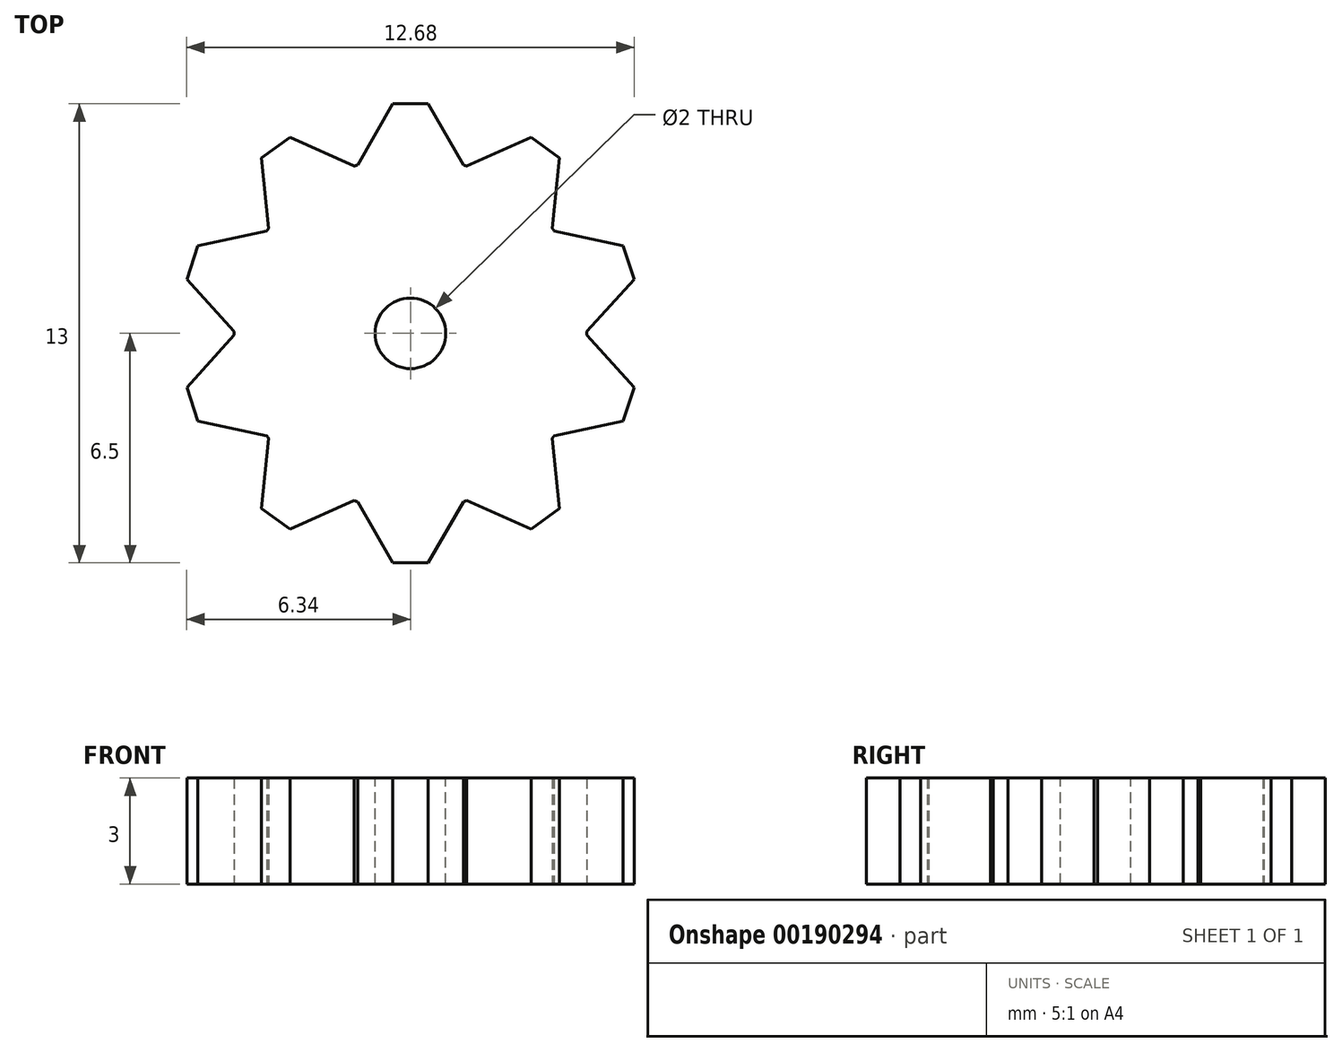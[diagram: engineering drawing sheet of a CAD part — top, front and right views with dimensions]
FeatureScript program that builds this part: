
annotation { "Feature Type Name" : "Feature", "Feature Type Description" : "" }
export const myFeature = defineFeature(function(context is Context, id is Id, definition is map)
    precondition{}
    {
        {
            var Q0;
            Q0=qCreatedBy(makeId("Top.planeOp"),FACE);
            var sketch = newSketch(context, id + "F0", { "sketchPlane" : qUnion([Q0])});
            skCircle(sketch, "E0", {"center": v(0, 0) * mm, "radius": 5 * mm});
            skLineSegment(sketch, "E1", {"start": v(0, 0) * mm, "end": v(0, 6.5) * mm, "construction": true});
            skLineSegment(sketch, "E2", {"start": v(0, 6.5) * mm, "end": v(-0.5, 6.5) * mm});
            skLineSegment(sketch, "E3", {"start": v(-0.5, 6.5) * mm, "end": v(-1.5, 4.77) * mm});
            skLineSegment(sketch, "E4.MirrorCS", {"start": v(0, 6.5) * mm, "end": v(0.5, 6.5) * mm});
            skLineSegment(sketch, "E5.MirrorCS", {"start": v(0.5, 6.5) * mm, "end": v(1.5, 4.77) * mm});
            skLineSegment(sketch, "E6.1.0", {"start": v(-4.23, 4.96) * mm, "end": v(-4.02, 2.98) * mm});
            skLineSegment(sketch, "E6.1.1", {"start": v(-3.82, 5.26) * mm, "end": v(-4.23, 4.96) * mm});
            skLineSegment(sketch, "E6.1.2", {"start": v(-3.82, 5.26) * mm, "end": v(-3.42, 5.55) * mm});
            skLineSegment(sketch, "E6.1.3", {"start": v(-3.42, 5.55) * mm, "end": v(-1.6, 4.74) * mm});
            skLineSegment(sketch, "E6.2.0", {"start": v(-6.34, 1.53) * mm, "end": v(-5, 0.05) * mm});
            skLineSegment(sketch, "E6.2.1", {"start": v(-6.18, 2) * mm, "end": v(-6.34, 1.53) * mm});
            skLineSegment(sketch, "E6.2.2", {"start": v(-6.18, 2) * mm, "end": v(-6.03, 2.48) * mm});
            skLineSegment(sketch, "E6.2.3", {"start": v(-6.03, 2.48) * mm, "end": v(-4.07, 2.9) * mm});
            skLineSegment(sketch, "E7.2.3.0", {"start": v(-6.03, -2.48) * mm, "end": v(-4.07, -2.9) * mm});
            skLineSegment(sketch, "E7.3.3.0", {"start": v(-6.18, -2) * mm, "end": v(-6.03, -2.48) * mm});
            skLineSegment(sketch, "E7.6.3.0", {"start": v(-6.18, -2) * mm, "end": v(-6.34, -1.53) * mm});
            skLineSegment(sketch, "E7.9.3.0", {"start": v(-6.34, -1.53) * mm, "end": v(-5, -0.05) * mm});
            skLineSegment(sketch, "E7.2.4.0", {"start": v(-3.42, -5.55) * mm, "end": v(-1.6, -4.74) * mm});
            skLineSegment(sketch, "E7.3.4.0", {"start": v(-3.82, -5.26) * mm, "end": v(-3.42, -5.55) * mm});
            skLineSegment(sketch, "E7.6.4.0", {"start": v(-3.82, -5.26) * mm, "end": v(-4.23, -4.96) * mm});
            skLineSegment(sketch, "E7.9.4.0", {"start": v(-4.23, -4.96) * mm, "end": v(-4.02, -2.98) * mm});
            skLineSegment(sketch, "E7.2.5.0", {"start": v(0.5, -6.5) * mm, "end": v(1.5, -4.77) * mm});
            skLineSegment(sketch, "E7.3.5.0", {"start": v(0, -6.5) * mm, "end": v(0.5, -6.5) * mm});
            skLineSegment(sketch, "E7.6.5.0", {"start": v(0, -6.5) * mm, "end": v(-0.5, -6.5) * mm});
            skLineSegment(sketch, "E7.9.5.0", {"start": v(-0.5, -6.5) * mm, "end": v(-1.5, -4.77) * mm});
            skLineSegment(sketch, "E7.2.6.0", {"start": v(4.23, -4.96) * mm, "end": v(4.02, -2.98) * mm});
            skLineSegment(sketch, "E7.3.6.0", {"start": v(3.82, -5.26) * mm, "end": v(4.23, -4.96) * mm});
            skLineSegment(sketch, "E7.6.6.0", {"start": v(3.82, -5.26) * mm, "end": v(3.42, -5.55) * mm});
            skLineSegment(sketch, "E7.9.6.0", {"start": v(3.42, -5.55) * mm, "end": v(1.6, -4.74) * mm});
            skLineSegment(sketch, "E7.2.7.0", {"start": v(6.34, -1.53) * mm, "end": v(5, -0.05) * mm});
            skLineSegment(sketch, "E7.3.7.0", {"start": v(6.18, -2) * mm, "end": v(6.34, -1.53) * mm});
            skLineSegment(sketch, "E7.6.7.0", {"start": v(6.18, -2) * mm, "end": v(6.03, -2.48) * mm});
            skLineSegment(sketch, "E7.9.7.0", {"start": v(6.03, -2.48) * mm, "end": v(4.07, -2.9) * mm});
            skLineSegment(sketch, "E7.2.8.0", {"start": v(6.03, 2.48) * mm, "end": v(4.07, 2.9) * mm});
            skLineSegment(sketch, "E7.3.8.0", {"start": v(6.18, 2) * mm, "end": v(6.03, 2.48) * mm});
            skLineSegment(sketch, "E7.6.8.0", {"start": v(6.18, 2) * mm, "end": v(6.34, 1.53) * mm});
            skLineSegment(sketch, "E7.9.8.0", {"start": v(6.34, 1.53) * mm, "end": v(5, 0.05) * mm});
            skLineSegment(sketch, "E7.2.9.0", {"start": v(3.42, 5.55) * mm, "end": v(1.6, 4.74) * mm});
            skLineSegment(sketch, "E7.3.9.0", {"start": v(3.82, 5.26) * mm, "end": v(3.42, 5.55) * mm});
            skLineSegment(sketch, "E7.6.9.0", {"start": v(3.82, 5.26) * mm, "end": v(4.23, 4.96) * mm});
            skLineSegment(sketch, "E7.9.9.0", {"start": v(4.23, 4.96) * mm, "end": v(4.02, 2.98) * mm});
            skSolve(sketch);
        }
        {
            var Q0;
            Q0 = qSketchRegion(id + "F0", true);
            extrude(context, id + "F1", {"entities" : qUnion([Q0]), "depth" : 3 * mm});
        }
        {
            var Q0;
            Q0=makeQuery(id+"F1.opExtrude","CAP_FACE",FACE,{"disambiguationData":[OSD([sQuery(id+"F0.wireOp",EDGE,"E0"),sQuery(id+"F0.wireOp",EDGE,"E2"),sQuery(id+"F0.wireOp",EDGE,"E3"),sQuery(id+"F0.wireOp",EDGE,"E4.MirrorCS"),sQuery(id+"F0.wireOp",EDGE,"E5.MirrorCS"),sQuery(id+"F0.wireOp",EDGE,"E6.1.0"),sQuery(id+"F0.wireOp",EDGE,"E6.1.1"),sQuery(id+"F0.wireOp",EDGE,"E6.1.2"),sQuery(id+"F0.wireOp",EDGE,"E6.1.3"),sQuery(id+"F0.wireOp",EDGE,"E6.2.0"),sQuery(id+"F0.wireOp",EDGE,"E6.2.1"),sQuery(id+"F0.wireOp",EDGE,"E6.2.2"),sQuery(id+"F0.wireOp",EDGE,"E6.2.3"),sQuery(id+"F0.wireOp",EDGE,"E7.2.3.0"),sQuery(id+"F0.wireOp",EDGE,"E7.3.3.0"),sQuery(id+"F0.wireOp",EDGE,"E7.6.3.0"),sQuery(id+"F0.wireOp",EDGE,"E7.9.3.0"),sQuery(id+"F0.wireOp",EDGE,"E7.2.4.0"),sQuery(id+"F0.wireOp",EDGE,"E7.3.4.0"),sQuery(id+"F0.wireOp",EDGE,"E7.6.4.0"),sQuery(id+"F0.wireOp",EDGE,"E7.9.4.0"),sQuery(id+"F0.wireOp",EDGE,"E7.2.5.0"),sQuery(id+"F0.wireOp",EDGE,"E7.3.5.0"),sQuery(id+"F0.wireOp",EDGE,"E7.6.5.0"),sQuery(id+"F0.wireOp",EDGE,"E7.9.5.0"),sQuery(id+"F0.wireOp",EDGE,"E7.2.6.0"),sQuery(id+"F0.wireOp",EDGE,"E7.3.6.0"),sQuery(id+"F0.wireOp",EDGE,"E7.6.6.0"),sQuery(id+"F0.wireOp",EDGE,"E7.9.6.0"),sQuery(id+"F0.wireOp",EDGE,"E7.2.7.0"),sQuery(id+"F0.wireOp",EDGE,"E7.3.7.0"),sQuery(id+"F0.wireOp",EDGE,"E7.6.7.0"),sQuery(id+"F0.wireOp",EDGE,"E7.9.7.0"),sQuery(id+"F0.wireOp",EDGE,"E7.2.8.0"),sQuery(id+"F0.wireOp",EDGE,"E7.3.8.0"),sQuery(id+"F0.wireOp",EDGE,"E7.6.8.0"),sQuery(id+"F0.wireOp",EDGE,"E7.9.8.0"),sQuery(id+"F0.wireOp",EDGE,"E7.2.9.0"),sQuery(id+"F0.wireOp",EDGE,"E7.3.9.0"),sQuery(id+"F0.wireOp",EDGE,"E7.6.9.0"),sQuery(id+"F0.wireOp",EDGE,"E7.9.9.0")])],"isStart":false});
            var sketch = newSketch(context, id + "F2", { "sketchPlane" : qUnion([Q0])});
            skCircle(sketch, "E8", {"center": v(0, 0) * mm, "radius": 1 * mm});
            skSolve(sketch);
        }
        {
            var Q0;
            Q0 = qSketchRegion(id + "F2", true);
            extrude(context, id + "F3", {"entities" : qUnion([Q0]), "operationType" : NewBodyOperationType.REMOVE, "endBound" : BoundingType.UP_TO_NEXT, "oppositeDirection" : true, "depth" : 25 * mm});
        }
    });
